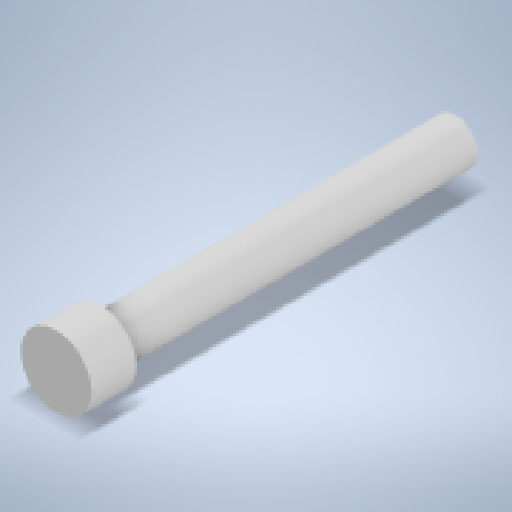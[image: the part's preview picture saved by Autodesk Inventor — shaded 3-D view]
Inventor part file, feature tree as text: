
AUTODESK INVENTOR PART (.ipt)
format: ipt  version: 2024 (Build 280153000, 153)  size: 146,432 bytes
history: native  units: mm
features: other x3, extrude x2, sketch x2, plane x1
ambient origin geometry x8: Origin, YZ Plane, XZ Plane, XY Plane, X Axis, Y Axis, Z Axis, Center Point
bodies: Solid1 (feature_tree)
feature tree (8):
  plane  "Work Plane1"
  extrude  "Extrusion1"  Depth=5.0mm TaperAngle=0.0deg
  extrude  "Extrusion2"  Depth=40.0mm TaperAngle=0.0deg
  sketch  "Sketch1"  dims[d0=8.0mm d1=5.0mm d2=0.0mm]
  sketch  "Sketch2"  dims[d3=5.0mm d4=40.0mm d5=0.0mm]
  other  "<userpath>\Documents\Inventor\robot arm\base_assembly.iam"
  other  "base_assembly.iam"
  other  "base-top-plate:1"
